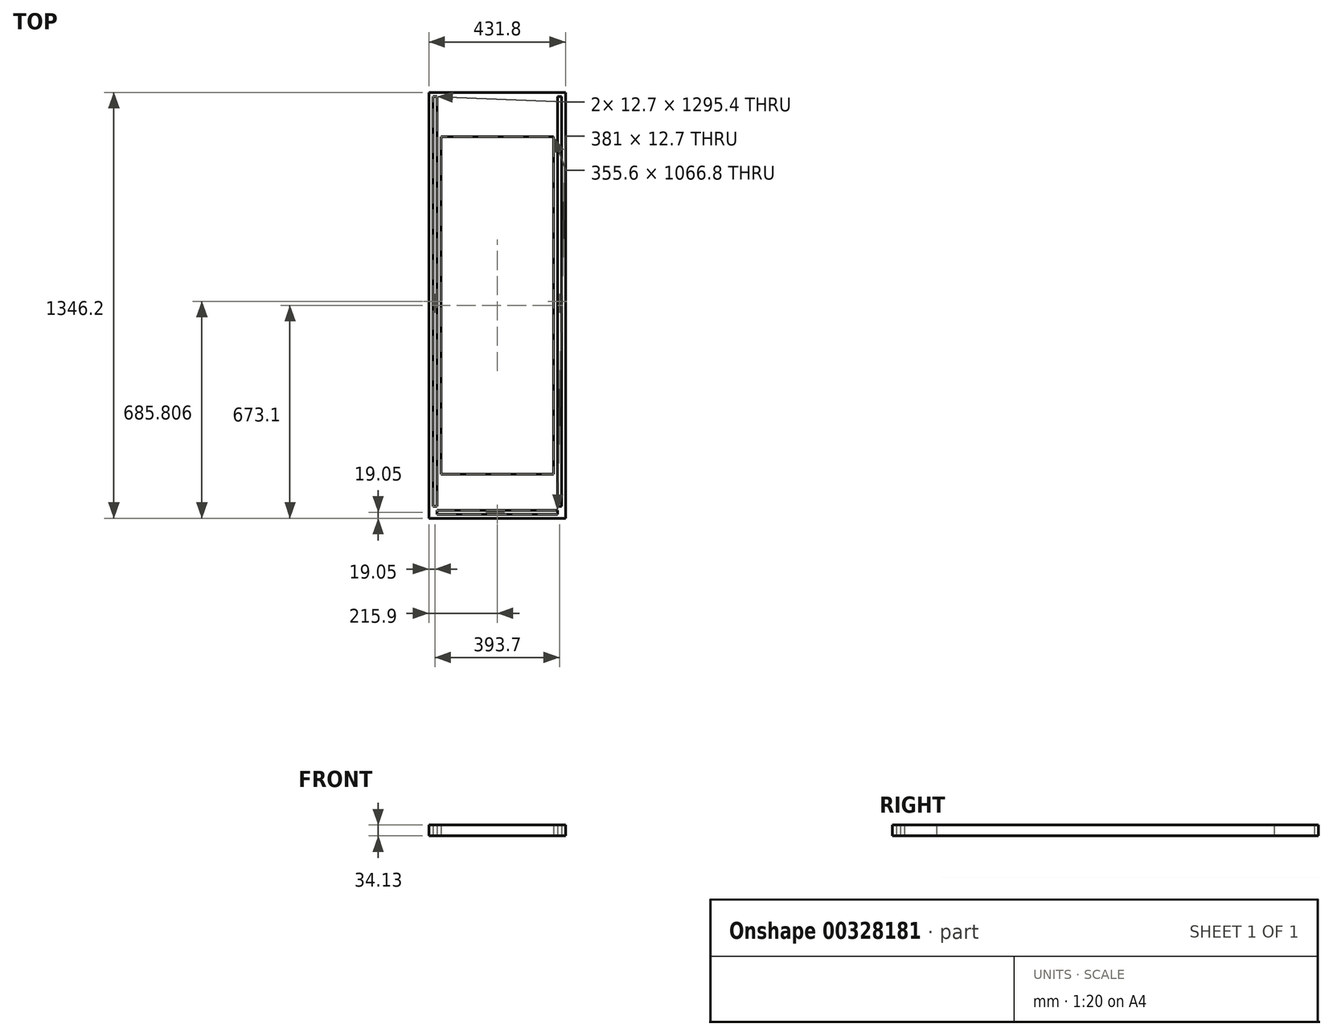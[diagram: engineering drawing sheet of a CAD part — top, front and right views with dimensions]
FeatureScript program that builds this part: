
annotation { "Feature Type Name" : "Feature", "Feature Type Description" : "" }
export const myFeature = defineFeature(function(context is Context, id is Id, definition is map)
    precondition{}
    {
        {
            var Q0;
            Q0=qCreatedBy(makeId("Top.planeOp"),FACE);
            var sketch = newSketch(context, id + "F0", { "sketchPlane" : qUnion([Q0])});
            skLineSegment(sketch, "E0.bottom", {"start": v(-215.9, 673.1) * mm, "end": v(215.9, 673.1) * mm});
            skLineSegment(sketch, "E0.top", {"start": v(-215.9, -673.1) * mm, "end": v(215.9, -673.1) * mm});
            skLineSegment(sketch, "E0.left", {"start": v(-215.9, 673.1) * mm, "end": v(-215.9, -673.1) * mm});
            skLineSegment(sketch, "E0.right", {"start": v(215.9, 673.1) * mm, "end": v(215.9, -673.1) * mm});
            skPoint(sketch, "E0.middle", {"position": v(0, 0) * mm});
            skLineSegment(sketch, "E1", {"start": v(0, -673.1) * mm, "end": v(0, -660.4) * mm});
            skPoint(sketch, "E1.endSnap0", {"position": v(0, -673.1) * mm});
            skLineSegment(sketch, "E2", {"start": v(0, -660.4) * mm, "end": v(190.5, -660.4) * mm});
            skLineSegment(sketch, "E3", {"start": v(0, -660.4) * mm, "end": v(-190.5, -660.4) * mm});
            skLineSegment(sketch, "E4", {"start": v(-190.5, -660.4) * mm, "end": v(-190.5, -647.7) * mm});
            skLineSegment(sketch, "E5", {"start": v(-190.5, -647.7) * mm, "end": v(190.5, -647.7) * mm});
            skLineSegment(sketch, "E6", {"start": v(190.5, -647.7) * mm, "end": v(190.5, -660.4) * mm});
            skLineSegment(sketch, "E7", {"start": v(215.9, 74.26) * mm, "end": v(203.2, 74.26) * mm});
            skLineSegment(sketch, "E8", {"start": v(-203.2, 660.4) * mm, "end": v(-203.2, -635) * mm});
            skLineSegment(sketch, "E9", {"start": v(203.2, 660.4) * mm, "end": v(203.2, -635) * mm});
            skLineSegment(sketch, "E10", {"start": v(-203.2, 660.4) * mm, "end": v(-190.5, 660.4) * mm});
            skLineSegment(sketch, "E11", {"start": v(203.2, 660.4) * mm, "end": v(190.5, 660.4) * mm});
            skLineSegment(sketch, "E12", {"start": v(-190.5, 660.4) * mm, "end": v(-190.5, -635) * mm});
            skLineSegment(sketch, "E13", {"start": v(-190.5, -635) * mm, "end": v(-203.2, -635) * mm});
            skLineSegment(sketch, "E14", {"start": v(190.5, 660.4) * mm, "end": v(190.5, -635) * mm});
            skLineSegment(sketch, "E15", {"start": v(190.5, -635) * mm, "end": v(203.2, -635) * mm});
            skLineSegment(sketch, "E16.bottom", {"start": v(177.8, 533.4) * mm, "end": v(-177.8, 533.4) * mm});
            skLineSegment(sketch, "E16.top", {"start": v(177.8, -533.4) * mm, "end": v(-177.8, -533.4) * mm});
            skLineSegment(sketch, "E16.left", {"start": v(177.8, 533.4) * mm, "end": v(177.8, -533.4) * mm});
            skLineSegment(sketch, "E16.right", {"start": v(-177.8, 533.4) * mm, "end": v(-177.8, -533.4) * mm});
            skSolve(sketch);
        }
        {
            var Q0;
            Q0=makeQuery(id+"F0.imprint","IMPRINT",FACE,{"disambiguationData":[TD([[makeQuery(id+"F0.imprint","IMPRINT",EDGE,{"derivedFrom":sQuery(id+"F0.wireOp",EDGE,"E0.bottom")}),-1.0]])]});
            extrude(context, id + "F1", {"entities" : qUnion([Q0]), "depth" : 8.73 * mm, "hasSecondDirection" : true, "secondDirectionOppositeDirection" : true, "secondDirectionDepth" : 25.4 * mm});
        }
    });
